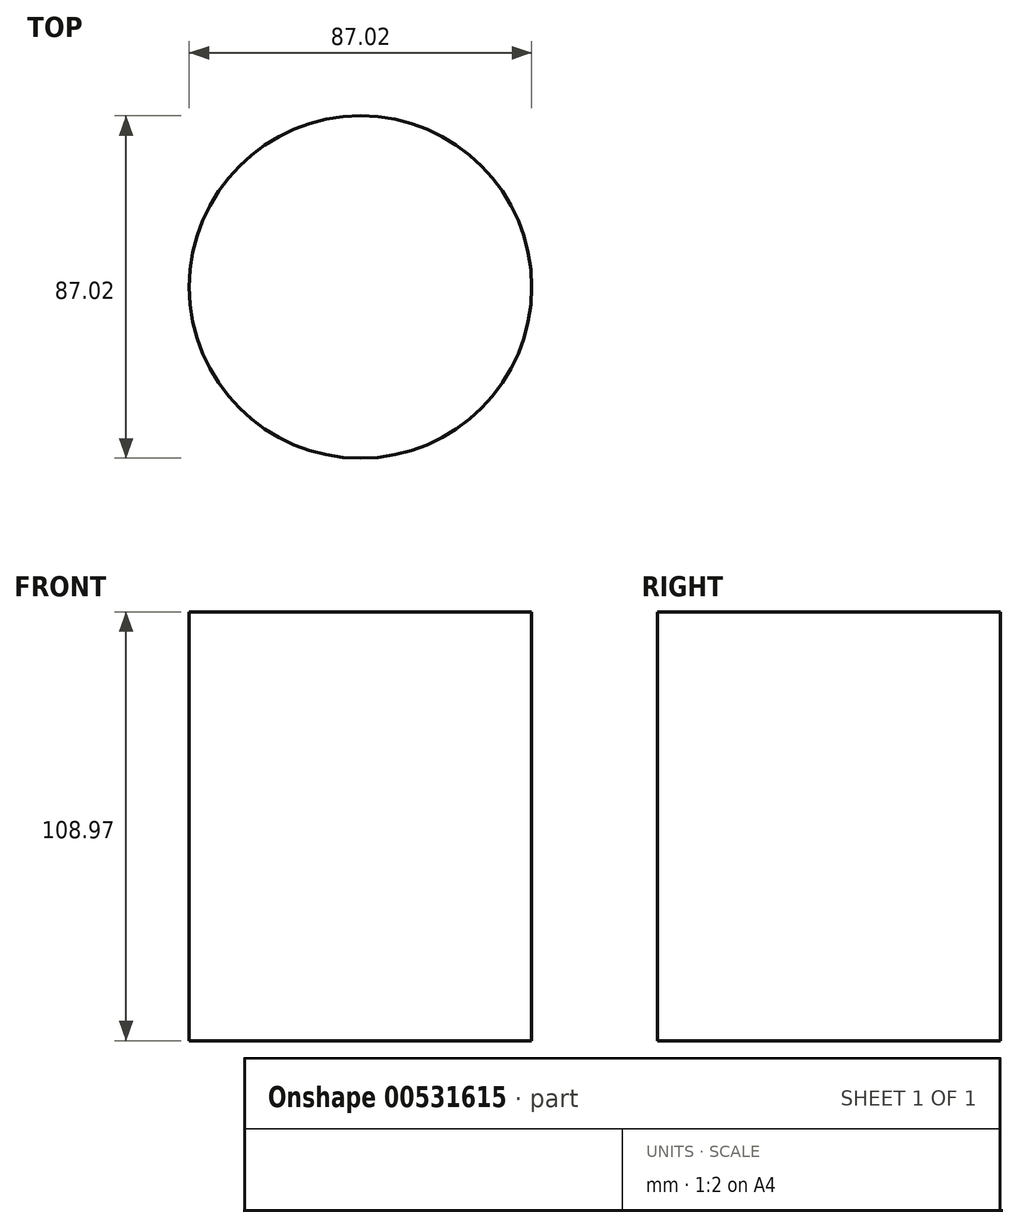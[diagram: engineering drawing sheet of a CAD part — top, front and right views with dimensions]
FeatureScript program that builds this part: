
annotation { "Feature Type Name" : "Feature", "Feature Type Description" : "" }
export const myFeature = defineFeature(function(context is Context, id is Id, definition is map)
    precondition{}
    {
        {
            var Q0;
            Q0=qCreatedBy(makeId("Top.planeOp"),FACE);
            var sketch = newSketch(context, id + "F0", { "sketchPlane" : qUnion([Q0])});
            skCircle(sketch, "E0", {"center": v(0, 0) * mm, "radius": 43.51 * mm});
            skSolve(sketch);
        }
        {
            var Q0;
            Q0 = qSketchRegion(id + "F0", true);
            extrude(context, id + "F1", {"entities" : qUnion([Q0]), "depth" : 108.97 * mm, "offsetDistance" : 25.4 * mm});
        }
    });
